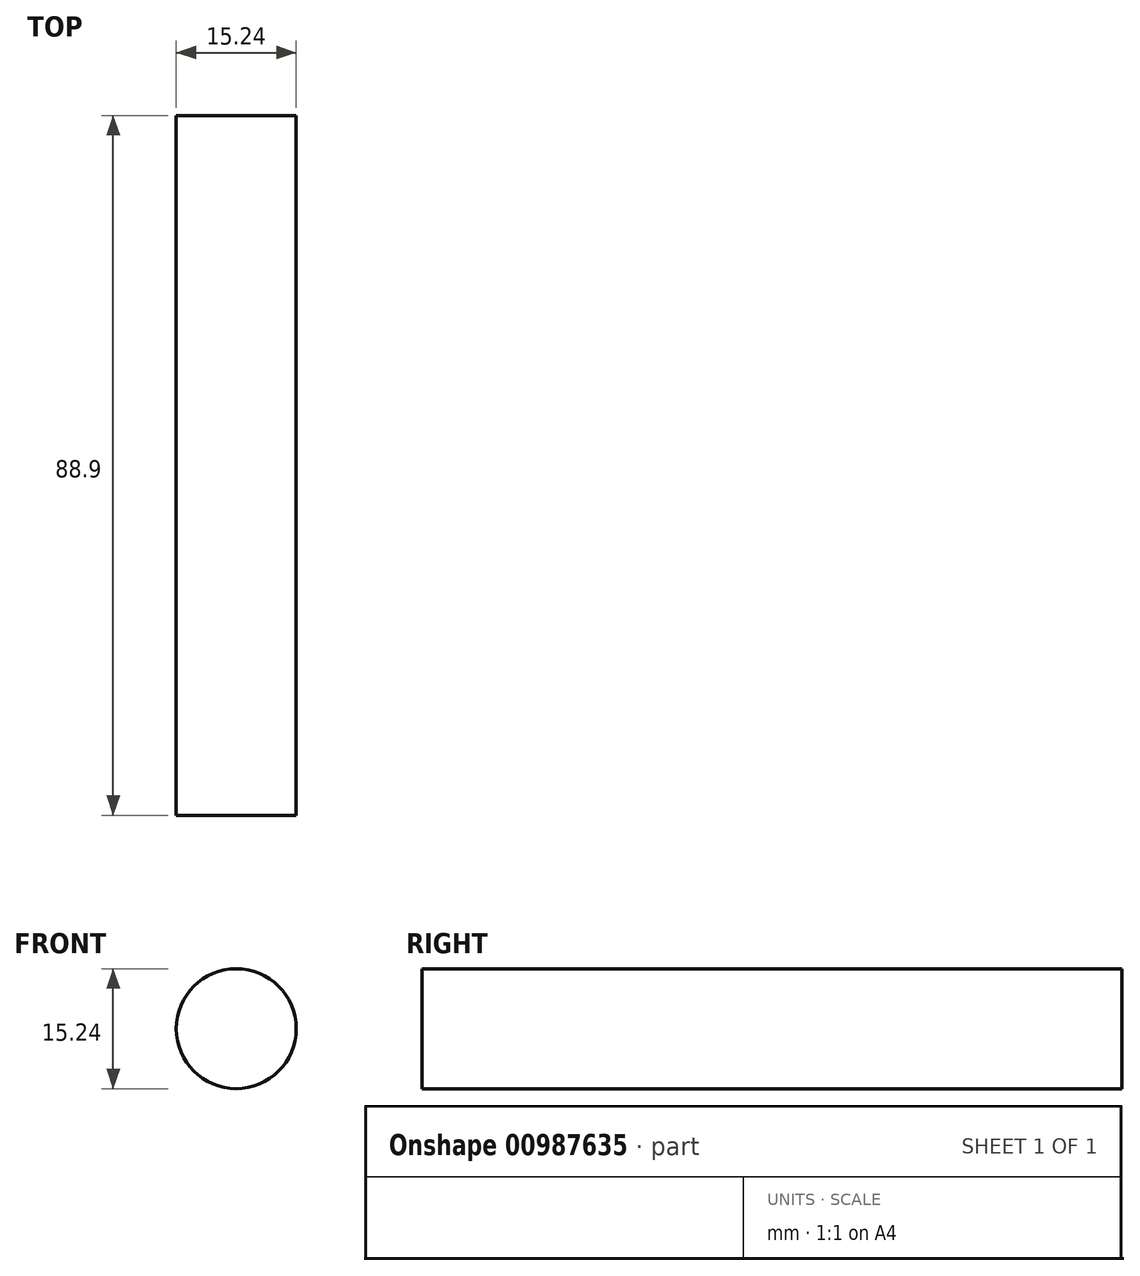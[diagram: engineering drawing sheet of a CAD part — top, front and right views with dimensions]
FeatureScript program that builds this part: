
annotation { "Feature Type Name" : "Feature", "Feature Type Description" : "" }
export const myFeature = defineFeature(function(context is Context, id is Id, definition is map)
    precondition{}
    {
        {
            var Q0;
            Q0=qCreatedBy(makeId("Front.planeOp"),FACE);
            var sketch = newSketch(context, id + "F0", { "sketchPlane" : qUnion([Q0])});
            skCircle(sketch, "E0", {"center": v(0, 0) * mm, "radius": 7.62 * mm});
            skSolve(sketch);
        }
        {
            var Q0;
            Q0=makeQuery(id+"F0.imprint","IMPRINT",FACE,{"disambiguationData":[TD([[makeQuery(id+"F0.imprint","IMPRINT",EDGE,{"derivedFrom":sQuery(id+"F0.wireOp",EDGE,"E0")}),1.0]])]});
            extrude(context, id + "F1", {"entities" : qUnion([Q0]), "depth" : 88.9 * mm, "offsetDistance" : 25.4 * mm});
        }
    });
